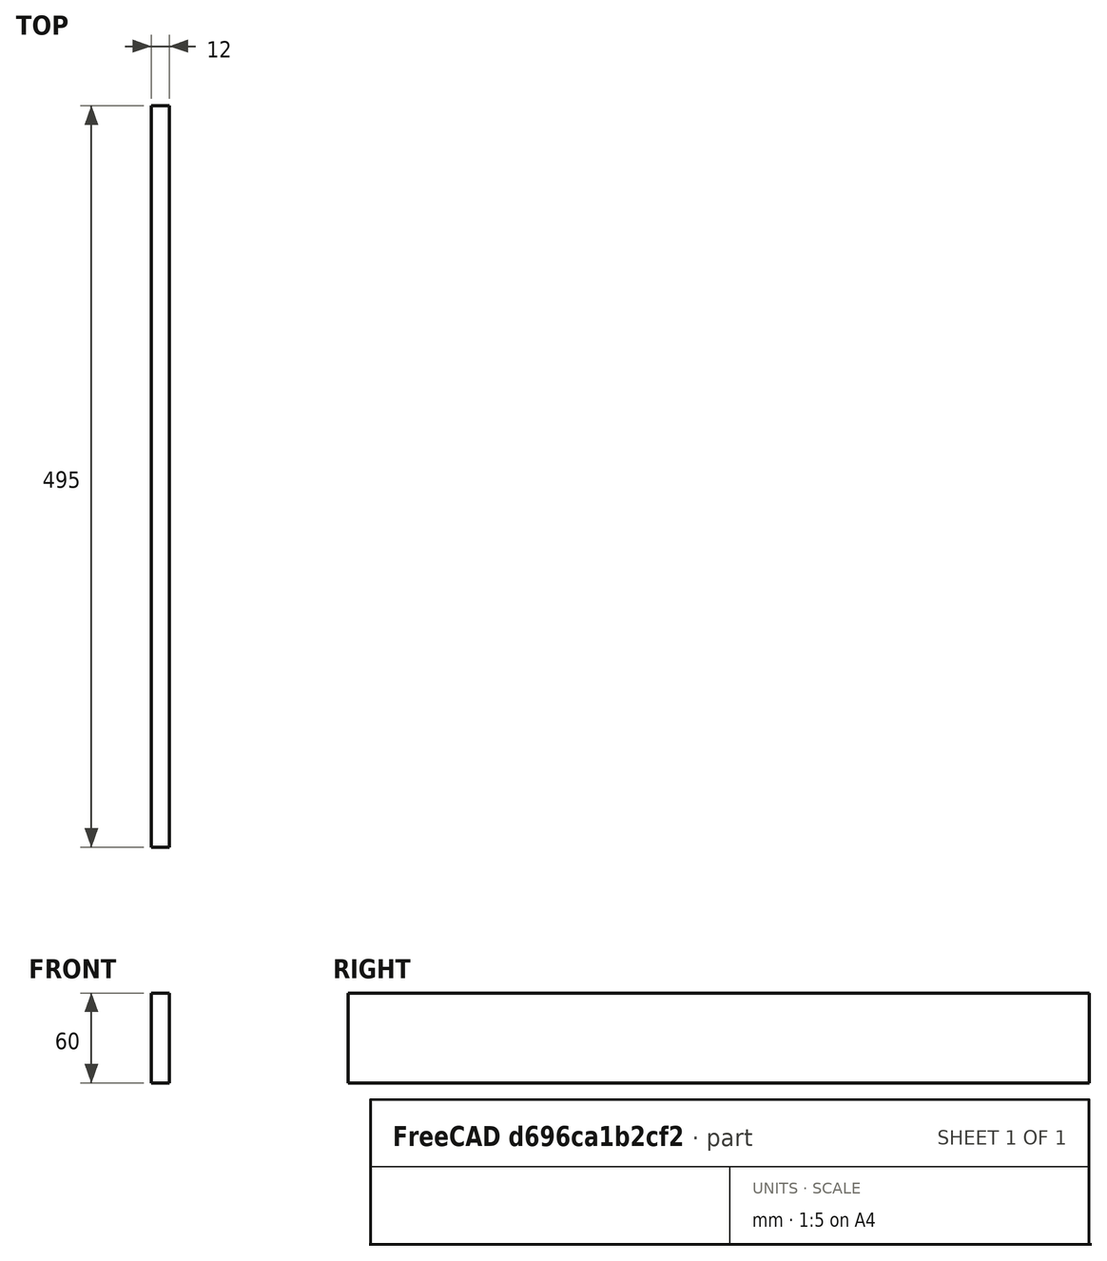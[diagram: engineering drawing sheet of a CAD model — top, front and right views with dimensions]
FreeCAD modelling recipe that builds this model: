
FCSTD DOCUMENT  (FreeCAD 0.19R24291 (Git))
Label: 8000_WindowFrameTop_
License: All rights reserved
LicenseURL: http://en.wikipedia.org/wiki/All_rights_reserved
objects: Sketcher::SketchObject×1, Spreadsheet::Sheet×1, PartDesign::Pad×1, PartDesign::Body×1
note: 4 computed .brp shape members not serialized (recipe doc carries the construction recipe); baked Part::Feature solids carry a one-line shape summary decoded from their .brp

FEATURE [Sketcher::SketchObject] Sketch
  FullyConstrained = true
  MapMode = 4
  Placement = pos=(0,0,0) rot=(0.57735,0.57735,0.57735;2.0944rad)
  Support = -> [XY_Plane]
  expr: Constraints[6] = Spreadsheet.nY
  expr: Constraints[5] = Spreadsheet.nZ
  sketch-geometry (5):
    g0: LineSegment StartX=0 StartY=0 StartZ=0 EndX=0 EndY=60 EndZ=0
    g1: LineSegment StartX=495 StartY=0 StartZ=0 EndX=495 EndY=60 EndZ=0
    g2: LineSegment StartX=495 StartY=60 StartZ=0 EndX=0 EndY=60 EndZ=0
    g3: LineSegment StartX=247.5 StartY=0 StartZ=0 EndX=0 EndY=0 EndZ=0
    g4: LineSegment StartX=495 StartY=0 StartZ=0 EndX=247.5 EndY=0 EndZ=0
  constraints (14):
    c: Vertical(g0)
    c: Vertical(g1)
    c: Coincident(g2,g1)
    c: Coincident(g2,g0)
    c: Horizontal(g2)
    c: DistanceY(g1,g1) = 60
    c: DistanceX(g2,g2) = 495
    c: Coincident(g3,g0)
    c: Coincident(g4,g1)
    c: Horizontal(g4)
    c: Equal(g3,g4)
    c: Coincident(g4,g3)
    c: Horizontal(g3)
    c: Coincident(g0,g-1)
FEATURE [Spreadsheet::Sheet] Spreadsheet  label="xls"
  cells = B2=BODY FLOOR; E2=Ex.Ref.; B3=Thichness; C3=.T; D3=12; E3=mm; B7=KEYBOARD FRONT; D7=Sperrholz Birke 12 mm; B8=Width; C8=nY; D8(nY)=495; B9=Height; C9=nZ; D9(nZ)=60; E9=F(T); B10=Thickness; C10=nT; D10(nT)=12
FEATURE [PartDesign::Pad] Pad
  AllowMultiFace = false
  Direction = (1,1,1)
  Length = 12
  Length2 = 100
  Profile = -> Sketch
  Reversed = true
  Type = 0
  expr: Length = Spreadsheet.nT
FEATURE [PartDesign::Body] Body
  Group = -> [Sketch,Pad]
  Origin = -> Origin
  Tip = -> Pad
